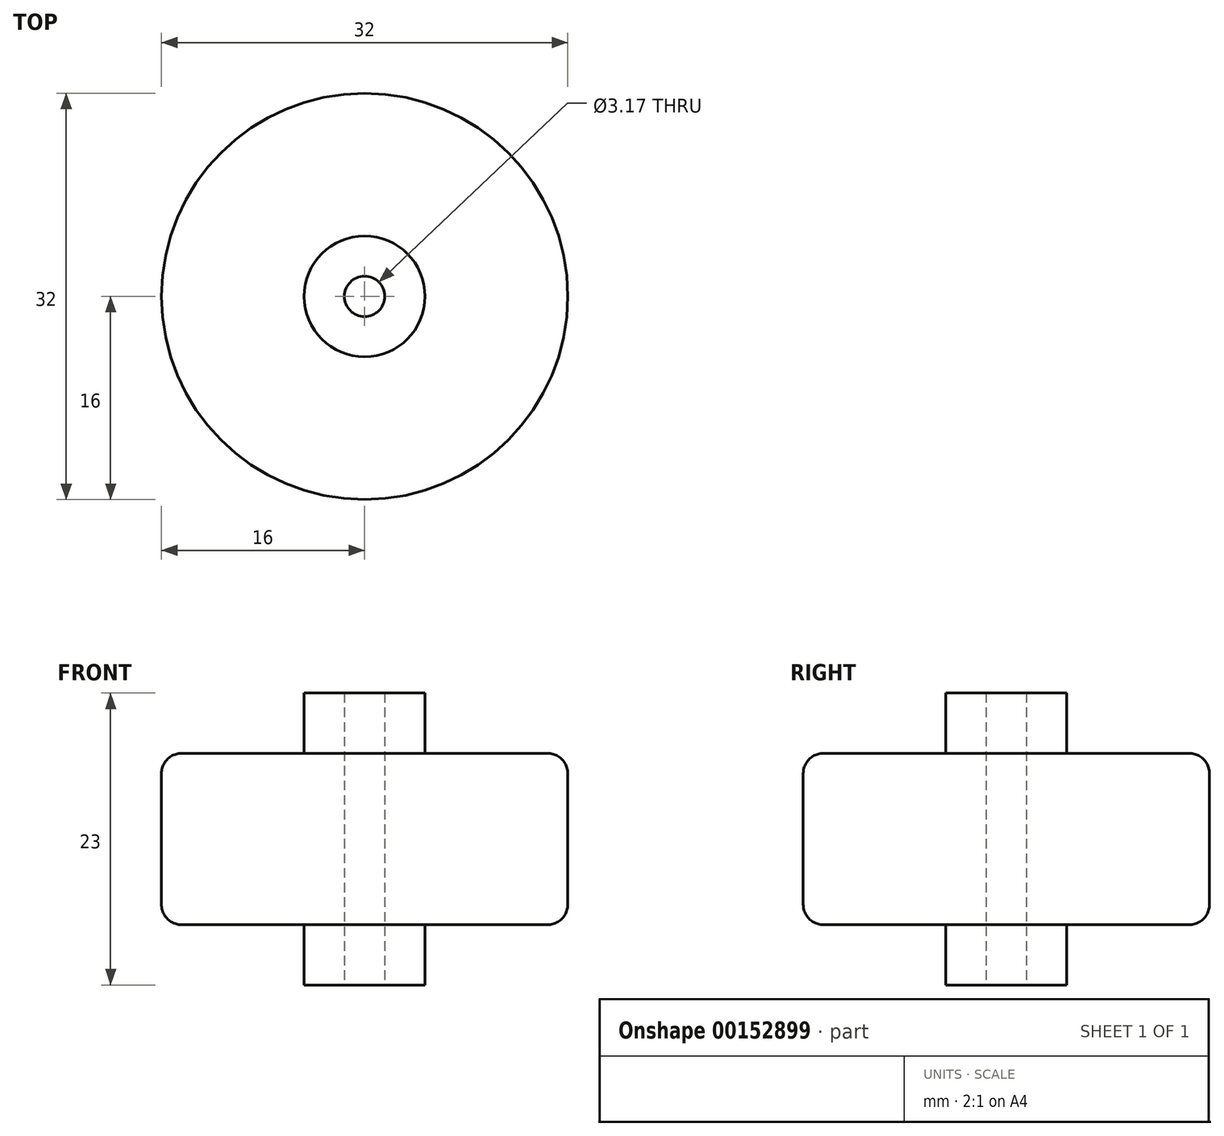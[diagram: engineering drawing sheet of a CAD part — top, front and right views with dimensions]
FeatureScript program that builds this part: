
annotation { "Feature Type Name" : "Feature", "Feature Type Description" : "" }
export const myFeature = defineFeature(function(context is Context, id is Id, definition is map)
    precondition{}
    {
        {
            var Q0;
            Q0=qCreatedBy(makeId("Top.planeOp"),FACE);
            var sketch = newSketch(context, id + "F0", { "sketchPlane" : qUnion([Q0])});
            skCircle(sketch, "E0", {"center": v(0, 0) * mm, "radius": 16 * mm});
            skCircle(sketch, "E1", {"center": v(0, 0) * mm, "radius": 1.59 * mm});
            skSolve(sketch);
        }
        {
            var Q0;
            Q0 = qSketchRegion(id + "F0", true);
            extrude(context, id + "F1", {"entities" : qUnion([Q0]), "endBound" : BoundingType.SYMMETRIC, "depth" : 13.5 * mm});
        }
        {
            var Q0;
            Q0=qCreatedBy(makeId("Top.planeOp"),FACE);
            var sketch = newSketch(context, id + "F2", { "sketchPlane" : qUnion([Q0])});
            skCircle(sketch, "E2", {"center": v(0, 0) * mm, "radius": 1.59 * mm});
            skCircle(sketch, "E3", {"center": v(0, 0) * mm, "radius": 4.76 * mm});
            skSolve(sketch);
        }
        {
            var Q0;
            Q0 = qSketchRegion(id + "F2", true);
            extrude(context, id + "F3", {"entities" : qUnion([Q0]), "operationType" : NewBodyOperationType.ADD, "endBound" : BoundingType.SYMMETRIC, "depth" : 23 * mm});
        }
        {
            var Q0;
            Q0=makeQuery(id+"F1.opExtrude","CAP_EDGE",EDGE,{"disambiguationData":[OSD([sQuery(id+"F0.wireOp",EDGE,"E0")])],"isStart":false});
            var Q1;
            Q1=makeQuery(id+"F1.opExtrude","CAP_EDGE",EDGE,{"disambiguationData":[OSD([sQuery(id+"F0.wireOp",EDGE,"E0")])],"isStart":true});
            fillet(context, id + "F4", {"entities" : qUnion([Q0, Q1]), "radius" : 1.59 * mm, "tangentPropagation" : true, "allowEdgeOverflow" : false});
        }
    });
